# Revit family: RAUPIANO PLUS Single Branch
name_source: partatom
category: Pipe Fittings
revit_build: Autodesk Revit MEP 2012 (Build: 20110309_2315(x64)
units: mm (PartAtom-declared; Revit-internal decimal feet)

## types (1)
- Standard
    A1 = 123104-001
    A10 = 123284-001
    A11 = 123834-001
    A12 = 123844-001
    A13 = 123294-001
    A14 = 121304-001
    A15 = 121324-001
    A16 = 121334-001
    A17 = 121344-001
    A18 = 122984-001
    A19 = 120574-001
    A2 = 123114-001
    A20 = 120594-001
    A21 = 120584-001
    A22 = 120604-001
    A23 = 124037-001
    A24 = 121744-003
    A25 = 121754-002
    A26 = 121764-002
    A27 = 124038-001
    A28 = 121784-001
    A29 = 123694-001
    A3 = 121234-001
    A30 = 123704-001
    A31 = 123964-001
    A4 = 121254-001
    A5 = 121264-001
    A6 = 121284-001
    A7 = 121294-001
    A8 = 121544-001
    A9 = 123274-001
    Description = REHAU RAUPIANO PLUS single branch
    Fail = No article found
    K Coefficient Table = Converging/Diverging Tee/Wye
    Lookup Table Name = RAUPIANO Single Branch.csv
    Loss Method = K Coefficient from Table
    M1 = 11231041001
    M10 = 11232841001
    M11 = 11238341001
    M12 = 11238441001
    M13 = 11232941001
    M14 = 11213041001
    M15 = 11213241001
    M16 = 11213341001
    M17 = 11213441001
    M18 = 11229841001
    M19 = 11205741001
    M2 = 11231141001
    M20 = 11205941001
    M21 = 11205841001
    M22 = 11206041001
    M23 = 11240371001
    M24 = 11217441003
    M25 = 11217541002
    M26 = 11217641002
    M27 = 11240381001
    M28 = 11217841001
    M29 = 11236941001
    M3 = 11212341001
    M30 = 11237041001
    M31 = 11239641001
    M4 = 11212541001
    M5 = 11212641001
    M6 = 11212841001
    M7 = 11212941001
    M8 = 11215441001
    M9 = 11232741001
    Manufacturer = REHAU
    T1 = DN 40/40 - 45 degree
    T10 = DN 90/50 - 87 degree
    T11 = DN 90/75 - 45 degree
    T12 = DN 90/75 - 87 degree
    T13 = DN 90/90 - 45 degree
    T14 = DN 110/50 - 45 degree
    T15 = DN 110/50 - 87 degree
    T16 = DN 110/75 - 45 degree
    T17 = DN 110/75 - 87 degree
    T18 = DN 110/110 - 45 degree
    T19 = DN 125/110 - 45 degree
    T2 = DN 40/40 - 87 degree
    T20 = DN 125/110 - 87 degree
    T21 = DN 125/125 - 45 degree
    T22 = DN 125/125 - 87 degree
    T23 = DN 160/110 - 45 degree
    T24 = DN 160/110 - 87 degree
    T25 = DN 160/125 - 45 degree
    T26 = DN 160/125 - 87 degree
    T27 = DN 160/160 - 45 degree
    T28 = DN 160/160 - 87 degree
    T29 = DN 200/160 - 45 degree
    T3 = DN 50/50 - 45 degree
    T30 = DN 200/160 - 87 degree
    T31 = DN 200/200 - 45 degree
    T4 = DN 50/50 - 87 degree
    T5 = DN 75/50 - 45 degree
    T6 = DN 75/50 - 87 degree
    T7 = DN 75/75 - 45 degree
    T8 = DN 75/75 - 87 degree
    T9 = DN 90/50 - 45 degree
    Type Comments = RAU-PP; Push-fit; White

## geometry (parser evidence)
native form markers: Sweep x5
no freeform markers — native parametric forms only
